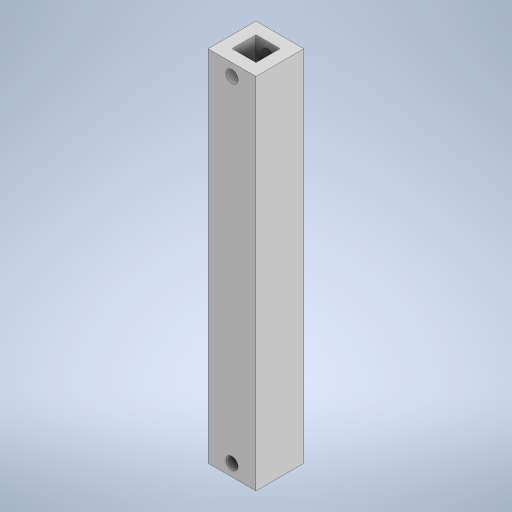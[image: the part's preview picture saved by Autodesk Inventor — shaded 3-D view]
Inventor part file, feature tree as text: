
AUTODESK INVENTOR PART (.ipt)
format: ipt  version: 2023 (Build 270158000, 158)  size: 247,296 bytes
history: native  units: mm
features: extrude x2, sketch x2
ambient origin geometry x8: Origin, YZ Plane, XZ Plane, XY Plane, X Axis, Y Axis, Z Axis, Center Point
bodies: Solido1 (feature_tree)
feature tree (4):
  extrude  "Estrusione1"  Depth=20.0mm
  extrude  "Estrusione2"  Depth=5.0mm
  sketch  "Schizzo2"
  sketch  "Schizzo3"
